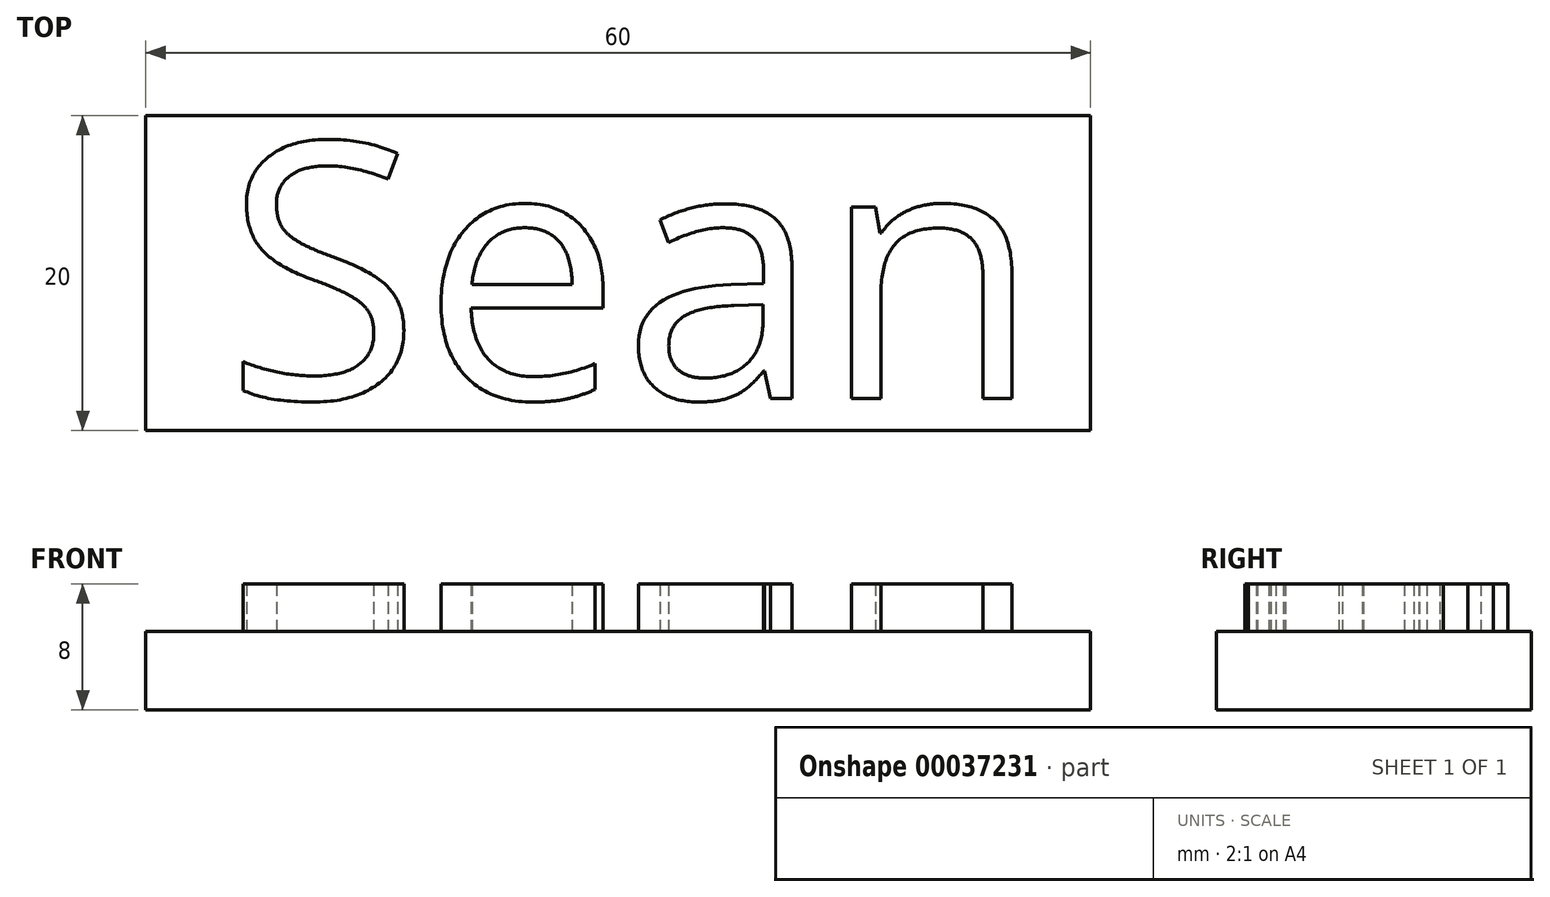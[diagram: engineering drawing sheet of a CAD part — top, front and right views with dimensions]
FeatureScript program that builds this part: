
annotation { "Feature Type Name" : "Feature", "Feature Type Description" : "" }
export const myFeature = defineFeature(function(context is Context, id is Id, definition is map)
    precondition{}
    {
        {
            var Q0;
            Q0=qCreatedBy(makeId("Top.planeOp"),FACE);
            var sketch = newSketch(context, id + "F0", { "sketchPlane" : qUnion([Q0])});
            skLineSegment(sketch, "E0.rect.bottom", {"start": v(30, 10) * mm, "end": v(-30, 10) * mm});
            skLineSegment(sketch, "E0.rect.top", {"start": v(30, -10) * mm, "end": v(-30, -10) * mm});
            skLineSegment(sketch, "E0.rect.left", {"start": v(30, 10) * mm, "end": v(30, -10) * mm});
            skLineSegment(sketch, "E0.rect.right", {"start": v(-30, 10) * mm, "end": v(-30, -10) * mm});
            skPoint(sketch, "E0.rect.middle", {"position": v(0, 0) * mm});
            skSolve(sketch);
        }
        {
            var Q0;
            Q0=makeQuery(id+"F0.imprint","IMPRINT",FACE,{"disambiguationData":[TD([[makeQuery(id+"F0.imprint","IMPRINT",EDGE,{"derivedFrom":sQuery(id+"F0.wireOp",EDGE,"E0.rect.bottom")}),1.0]])]});
            extrude(context, id + "F1", {"entities" : qUnion([Q0]), "depth" : 5 * mm});
        }
        {
            var Q0;
            Q0=makeQuery(id+"F1.opExtrude","CAP_FACE",FACE,{"disambiguationData":[OSD([sQuery(id+"F0.wireOp",EDGE,"E0.rect.bottom"),sQuery(id+"F0.wireOp",EDGE,"E0.rect.top"),sQuery(id+"F0.wireOp",EDGE,"E0.rect.left"),sQuery(id+"F0.wireOp",EDGE,"E0.rect.right")])],"isStart":false});
            var sketch = newSketch(context, id + "F2", { "sketchPlane" : qUnion([Q0])});
            skText(sketch, "E1", { "text": "Sean", "fontName": "OpenSans-Regular.ttf"});
            const initialGuessF2  = {"E1": [-0.025, -0.00797, 1, 0, 0.01637]};
            skSetInitialGuess(sketch, initialGuessF2);
            skSolve(sketch);
        }
        {
            var Q0;
            Q0 = qSketchRegion(id + "F2", true);
            extrude(context, id + "F3", {"entities" : qUnion([Q0]), "operationType" : NewBodyOperationType.ADD, "depth" : 3 * mm});
        }
    });
